# Revit family: TAG1
name_source: partatom
category: Furniture
units: mm (PartAtom-declared; Revit-internal decimal feet)

## family parameters
Always vertical = Yes
Cut with Voids When Loaded = No
OmniClass Number = 23.40.20.00
OmniClass Title = General Furniture and Specialties
Render Appearance Source = Family Geometry
Room Calculation Point = No
Shared = No
Work Plane-Based = No

## types (1)
- CW004
    Default Elevation = 0 mm  [stored 0 ft]
    Description = 1 x LB LOUNGE, CORNER, 34 TALL, SOLID BASE, REAR OVERLAY, RIGHT, 4 x LB LOUNGE 2 SEAT 34"H X 48"W X 30" SOLID BASE, 1 x Juggle Chair, 4-Leg Swivel Base, Auto Return, 1 x CaseWorks Countertop Laminate 24Dx72W, 1 x CaseWorks Countertop Laminate 24Dx90W, 1 x CaseWorks Toe Kick 04Hx54W (Cut to size on-site), 1 x CaseWorks Toe Kick 04Hx90W (Cut to size on-site), 3 x CaseWorks Base Cabinet Double Doors 33Hx30Wx24D, 1 x CaseWorks Base Appliance Garage Cabinet 33Hx18Wx24D, 1 x CaseWorks Base Cabinet Open 33Hx30Wx24D, 1 x CaseWorks Base Cabinet Trash Pullout 33Hx24Wx24D, 6 x 86 Degree Hinge Restriction Clip, 1 x TBL, RND, 2mm, 36Dx29H, DISC, GLD, 6 x Soft Close Mechanism for Hinged Doors
    Exported From CET Designer = Yes
    Manufacturer = AIS
    Model = F-SCCR343030R
    Show CW004 = Yes
    VisibilityIndex = 0

note: [stored X ft] marks values corroborated as IEEE doubles in the binary element streams (Revit-internal decimal feet)

## geometry (parser evidence)
native form markers: Sweep x3
no freeform markers — native parametric forms only
